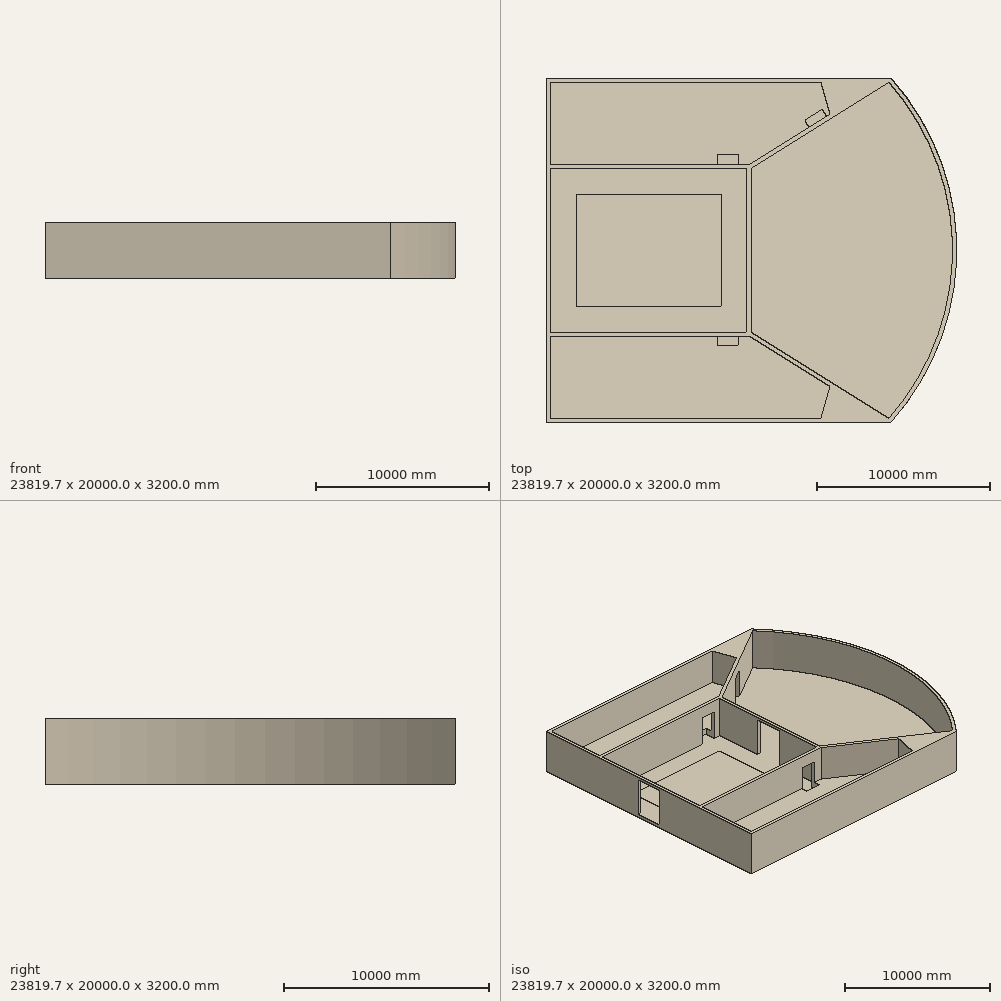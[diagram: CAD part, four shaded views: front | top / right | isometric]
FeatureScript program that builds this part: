
annotation { "Feature Type Name" : "Feature", "Feature Type Description" : "" }
export const myFeature = defineFeature(function(context is Context, id is Id, definition is map)
    precondition{}
    {
        {
            var Q0;
            Q0=qCreatedBy(makeId("Top.planeOp"),FACE);
            var sketch = newSketch(context, id + "F0", { "sketchPlane" : qUnion([Q0])});
            skLineSegment(sketch, "E0.bottom", {"start": v(0, 0) * mm, "end": v(20000, 0) * mm});
            skLineSegment(sketch, "E0.top", {"start": v(0, 20000) * mm, "end": v(20000, 20000) * mm});
            skLineSegment(sketch, "E0.left", {"start": v(0, 0) * mm, "end": v(0, 20000) * mm});
            skLineSegment(sketch, "E0.right", {"start": v(20000, 0) * mm, "end": v(20000, 20000) * mm});
            skLineSegment(sketch, "E1", {"start": v(20000, 10000) * mm, "end": v(8819.66, 10000) * mm});
            skCircle(sketch, "E2", {"center": v(8819.66, 10000) * mm, "radius": 15000 * mm});
            skSolve(sketch);
        }
        {
            var Q0;
            {var subQ2=sQuery(id+"F0.wireOp",EDGE,"E0.bottom");Q0=makeQuery(id+"F0.imprint","IMPRINT",FACE,{"disambiguationData":[TD([[makeQuery(id+"F0.imprint","IMPRINT",EDGE,{"derivedFrom":subQ2}),1.0]])]});}
            var Q1;
            {var subQ1=sQuery(id+"F0.wireOp",EDGE,"E0.right");var subQ3=makeQuery(id+"F0.imprint","IMPRINT",VERTEX,{"derivedFrom":subQ1});Q1=makeQuery(id+"F0.imprint","IMPRINT",FACE,{"disambiguationData":[TD([[makeQuery(id+"F0.imprint","IMPRINT",EDGE,{"disambiguationData":[TD([[subQ3,1.0]])],"derivedFrom":subQ1}),-1.0]])]});}
            extrude(context, id + "F1", {"entities" : qUnion([Q0, Q1]), "depth" : 3200 * mm});
        }
        {
            var Q0;
            Q0=makeQuery(id+"F1.opExtrude","CAP_FACE",FACE,{"disambiguationData":[OSD([sQuery(id+"F0.wireOp",EDGE,"E0.bottom"),sQuery(id+"F0.wireOp",EDGE,"E0.top"),sQuery(id+"F0.wireOp",EDGE,"E0.left"),sQuery(id+"F0.wireOp",EDGE,"E2")])],"isStart":false});
            var sketch = newSketch(context, id + "F2", { "sketchPlane" : qUnion([Q0])});
            skLineSegment(sketch, "E3.0", {"start": v(250, 250) * mm, "end": v(19887.63, 250) * mm});
            skLineSegment(sketch, "E3.1", {"start": v(250, 19750) * mm, "end": v(250, 250) * mm});
            skLineSegment(sketch, "E3.2", {"start": v(19887.63, 19750) * mm, "end": v(250, 19750) * mm});
            skArc(sketch, "E3.3", {"start": v(19887.63, 250) * mm, "mid": v(23569.66, 10000) * mm, "end": v(19887.63, 19750) * mm});
            skLineSegment(sketch, "E4", {"start": v(19887.63, 19750) * mm, "end": v(11887.63, 14750) * mm});
            skLineSegment(sketch, "E5", {"start": v(11887.63, 14750) * mm, "end": v(11887.63, 5250) * mm});
            skLineSegment(sketch, "E6", {"start": v(11887.63, 5250) * mm, "end": v(19887.63, 250) * mm});
            skLineSegment(sketch, "E7", {"start": v(11887.63, 14750) * mm, "end": v(250, 14750) * mm});
            skLineSegment(sketch, "E8", {"start": v(11887.63, 5250) * mm, "end": v(250, 5250) * mm});
            skLineSegment(sketch, "E9.0", {"start": v(11815.93, 15000) * mm, "end": v(250, 15000) * mm});
            skLineSegment(sketch, "E9.1", {"start": v(19415.93, 19750) * mm, "end": v(11815.93, 15000) * mm});
            skLineSegment(sketch, "E10.0", {"start": v(11815.93, 5000) * mm, "end": v(250, 5000) * mm});
            skLineSegment(sketch, "E10.1", {"start": v(11815.93, 5000) * mm, "end": v(19415.93, 250) * mm});
            skLineSegment(sketch, "E11.0", {"start": v(11637.63, 14750) * mm, "end": v(11637.63, 5250) * mm});
            skSolve(sketch);
        }
        {
            var Q0;
            Q0=makeQuery(id+"F2.imprint","IMPRINT",FACE,{"disambiguationData":[TD([[makeQuery(id+"F2.imprint","IMPRINT",EDGE,{"derivedFrom":sQuery(id+"F2.wireOp",EDGE,"E3.3")}),1.0]])]});
            var Q1;
            {var subQ5=sQuery(id+"F2.wireOp",EDGE,"E11.0");Q1=makeQuery(id+"F2.imprint","IMPRINT",FACE,{"disambiguationData":[TD([[makeQuery(id+"F2.imprint","IMPRINT",EDGE,{"derivedFrom":subQ5}),-1.0]])]});}
            extrude(context, id + "F3", {"entities" : qUnion([Q0, Q1]), "operationType" : NewBodyOperationType.REMOVE, "oppositeDirection" : true, "depth" : 2950 * mm});
        }
        {
            var Q0;
            {var subQ3=sQuery(id+"F2.wireOp",EDGE,"E9.0");Q0=makeQuery(id+"F2.imprint","IMPRINT",FACE,{"disambiguationData":[TD([[makeQuery(id+"F2.imprint","IMPRINT",EDGE,{"derivedFrom":subQ3}),-1.0]])]});}
            var Q1;
            {var subQ4=sQuery(id+"F2.wireOp",EDGE,"E10.0");Q1=makeQuery(id+"F2.imprint","IMPRINT",FACE,{"disambiguationData":[TD([[makeQuery(id+"F2.imprint","IMPRINT",EDGE,{"derivedFrom":subQ4}),1.0]])]});}
            extrude(context, id + "F4", {"entities" : qUnion([Q0, Q1]), "operationType" : NewBodyOperationType.REMOVE, "oppositeDirection" : true, "depth" : 2500 * mm});
        }
        {
            var Q0;
            Q0=makeQuery(id+"F1.opExtrude","SWEPT_FACE",FACE,{"disambiguationData":[OSD([sQuery(id+"F0.wireOp",EDGE,"E0.left")])]});
            var sketch = newSketch(context, id + "F5", { "sketchPlane" : qUnion([Q0])});
            skLineSegment(sketch, "E12", {"start": v(-10000, 0) * mm, "end": v(-10000, 1500) * mm});
            skLineSegment(sketch, "E13.bottom", {"start": v(-8950, 0) * mm, "end": v(-11050, 0) * mm});
            skLineSegment(sketch, "E13.top", {"start": v(-8950, 3000) * mm, "end": v(-11050, 3000) * mm});
            skLineSegment(sketch, "E13.left", {"start": v(-8950, 0) * mm, "end": v(-8950, 3000) * mm});
            skLineSegment(sketch, "E13.right", {"start": v(-11050, 0) * mm, "end": v(-11050, 3000) * mm});
            skPoint(sketch, "E13.middle", {"position": v(-10000, 1500) * mm});
            skLineSegment(sketch, "E14", {"start": v(-11050, 250) * mm, "end": v(-8950, 250) * mm});
            skSolve(sketch);
        }
        {
            var Q0;
            {var subQ5=sQuery(id+"F5.wireOp",EDGE,"E13.top");Q0=makeQuery(id+"F5.imprint","IMPRINT",FACE,{"disambiguationData":[TD([[makeQuery(id+"F5.imprint","IMPRINT",EDGE,{"derivedFrom":subQ5}),1.0]])]});}
            extrude(context, id + "F6", {"entities" : qUnion([Q0]), "operationType" : NewBodyOperationType.REMOVE, "oppositeDirection" : true, "depth" : 15000 * mm});
        }
        {
            var Q0;
            Q0=makeQuery(id+"F1.opExtrude","SWEPT_FACE",FACE,{"disambiguationData":[OSD([sQuery(id+"F0.wireOp",EDGE,"E0.left")])]});
            var sketch = newSketch(context, id + "F7", { "sketchPlane" : qUnion([Q0])});
            skLineSegment(sketch, "E15", {"start": v(-11050, 250) * mm, "end": v(-11050, 0) * mm});
            skLineSegment(sketch, "E16", {"start": v(-8950, 250) * mm, "end": v(-8950, 0) * mm});
            skLineSegment(sketch, "E17", {"start": v(-8950, 125) * mm, "end": v(-11050, 125) * mm});
            skSolve(sketch);
        }
        {
            var Q0;
            Q0=makeQuery(id+"F3.boolean.opBoolean","COPY",FACE,{"derivedFrom":makeQuery(id+"F3.opExtrude","SWEPT_FACE",FACE,{"disambiguationData":[OSD([sQuery(id+"F2.wireOp",EDGE,"E8")])]})});
            var sketch = newSketch(context, id + "F8", { "sketchPlane" : qUnion([Q0])});
            skLineSegment(sketch, "E18.bottom", {"start": v(-11137.63, 250) * mm, "end": v(-9937.63, 250) * mm});
            skLineSegment(sketch, "E18.top", {"start": v(-11137.63, 2350) * mm, "end": v(-9937.63, 2350) * mm});
            skLineSegment(sketch, "E18.left", {"start": v(-11137.63, 250) * mm, "end": v(-11137.63, 2350) * mm});
            skLineSegment(sketch, "E18.right", {"start": v(-9937.63, 250) * mm, "end": v(-9937.63, 2350) * mm});
            skSolve(sketch);
        }
        {
            var Q0;
            Q0 = qSketchRegion(id + "F8", true);
            extrude(context, id + "F9", {"entities" : qUnion([Q0]), "operationType" : NewBodyOperationType.REMOVE, "oppositeDirection" : true, "depth" : 750 * mm, "hasSecondDirection" : true, "secondDirectionOppositeDirection" : false, "secondDirectionDepth" : 10300 * mm});
        }
        {
            var Q0;
            Q0=makeQuery(id+"F1.opExtrude","SWEPT_FACE",FACE,{"disambiguationData":[OSD([sQuery(id+"F0.wireOp",EDGE,"E0.top")])]});
            var Q1;
            Q1=makeQuery(id+"F1.opExtrude","SWEPT_FACE",FACE,{"disambiguationData":[OSD([sQuery(id+"F0.wireOp",EDGE,"E0.bottom")])]});
            cPlane(context, id + "F10", {"entities" : qUnion([Q0, Q1]), "cplaneType" : CPlaneType.MID_PLANE, "offset" : 25 * mm, "width" : 150 * mm, "height" : 150 * mm});
        }
        {
            var Q0;
            Q0=makeQuery(id+"F3.boolean.opBoolean","COPY",FACE,{"derivedFrom":makeQuery(id+"F3.opExtrude","SWEPT_FACE",FACE,{"disambiguationData":[OSD([sQuery(id+"F2.wireOp",EDGE,"E4")])]})});
            var sketch = newSketch(context, id + "F11", { "sketchPlane" : qUnion([Q0])});
            skLineSegment(sketch, "E19", {"start": v(22615.17, 250) * mm, "end": v(22615.17, 1300) * mm});
            skLineSegment(sketch, "E20.bottom", {"start": v(22015.17, 250) * mm, "end": v(23215.17, 250) * mm});
            skLineSegment(sketch, "E20.top", {"start": v(22015.17, 2350) * mm, "end": v(23215.17, 2350) * mm});
            skLineSegment(sketch, "E20.left", {"start": v(22015.17, 250) * mm, "end": v(22015.17, 2350) * mm});
            skLineSegment(sketch, "E20.right", {"start": v(23215.17, 250) * mm, "end": v(23215.17, 2350) * mm});
            skPoint(sketch, "E20.middle", {"position": v(22615.17, 1300) * mm});
            skSolve(sketch);
        }
        {
            var Q0;
            Q0 = qSketchRegion(id + "F11", true);
            extrude(context, id + "F12", {"entities" : qUnion([Q0]), "operationType" : NewBodyOperationType.REMOVE, "oppositeDirection" : true, "depth" : 725 * mm});
        }
        {
            var Q0;
            {var subQ0=sQuery(id+"F11.wireOp",EDGE,"E20.bottom");Q0=makeQuery(id+"FxmqvzjOIRDMaaB_1.1.F12.boolean.opBoolean","MERGE",FACE,{"derivedFrom":[makeQuery(id+"F12.boolean.opBoolean","MERGE",FACE,{"derivedFrom":[makeQuery(id+"F9.boolean.opBoolean","MERGE",FACE,{"derivedFrom":[makeQuery(id+"F6.boolean.opBoolean","MERGE",FACE,{"derivedFrom":[makeQuery(id+"F3.boolean.opBoolean","COPY",FACE,{"derivedFrom":makeQuery(id+"F3.opExtrude","CAP_FACE",FACE,{"disambiguationData":[OSD([sQuery(id+"F2.wireOp",EDGE,"E3.1"),sQuery(id+"F2.wireOp",EDGE,"E7"),sQuery(id+"F2.wireOp",EDGE,"E8"),sQuery(id+"F2.wireOp",EDGE,"E11.0")])],"isStart":false})}),makeQuery(id+"F3.boolean.opBoolean","COPY",FACE,{"derivedFrom":makeQuery(id+"F3.opExtrude","CAP_FACE",FACE,{"disambiguationData":[OSD([sQuery(id+"F2.wireOp",EDGE,"E3.3"),sQuery(id+"F2.wireOp",EDGE,"E4"),sQuery(id+"F2.wireOp",EDGE,"E5"),sQuery(id+"F2.wireOp",EDGE,"E6")])],"isStart":false})}),makeQuery(id+"F6.opExtrude","SWEPT_FACE",FACE,{"disambiguationData":[OSD([sQuery(id+"F5.wireOp",EDGE,"E14")])]})]}),makeQuery(id+"F9.opExtrude","SWEPT_FACE",FACE,{"disambiguationData":[OSD([sQuery(id+"F8.wireOp",EDGE,"E18.bottom")])]})]}),makeQuery(id+"F12.opExtrude","SWEPT_FACE",FACE,{"disambiguationData":[OSD([subQ0])]})]}),makeQuery(id+"FxmqvzjOIRDMaaB_1.1.F12.opExtrude","SWEPT_FACE",FACE,{"disambiguationData":[OSD([subQ0])]})]});}
            var sketch = newSketch(context, id + "F13", { "sketchPlane" : qUnion([Q0])});
            skLineSegment(sketch, "E21.bottom", {"start": v(250, 14750) * mm, "end": v(11637.63, 14750) * mm});
            skLineSegment(sketch, "E21.top", {"start": v(250, 5250) * mm, "end": v(11637.63, 5250) * mm});
            skLineSegment(sketch, "E21.left", {"start": v(250, 14750) * mm, "end": v(250, 5250) * mm});
            skLineSegment(sketch, "E21.right", {"start": v(11637.63, 14750) * mm, "end": v(11637.63, 5250) * mm});
            skLineSegment(sketch, "E22.0", {"start": v(1750, 13250) * mm, "end": v(1750, 6750) * mm});
            skLineSegment(sketch, "E22.1", {"start": v(1750, 13250) * mm, "end": v(10137.63, 13250) * mm});
            skLineSegment(sketch, "E22.2", {"start": v(10137.63, 13250) * mm, "end": v(10137.63, 6750) * mm});
            skLineSegment(sketch, "E22.3", {"start": v(1750, 6750) * mm, "end": v(10137.63, 6750) * mm});
            skSolve(sketch);
        }
        {
            var Q0;
            Q0=makeQuery(id+"F13.imprint","IMPRINT",FACE,{"disambiguationData":[TD([[makeQuery(id+"F13.imprint","IMPRINT",EDGE,{"derivedFrom":sQuery(id+"F13.wireOp",EDGE,"E22.0")}),1.0]])]});
            extrude(context, id + "F14", {"entities" : qUnion([Q0]), "depth" : 15 * mm});
        }
        {
            var Q0;
            Q0=makeQuery(id+"F4.boolean.opBoolean","COPY",EDGE,{"derivedFrom":makeQuery(id+"F4.opExtrude","SWEPT_EDGE",EDGE,{"disambiguationData":[OSD([sQuery(id+"F2.wireOp",EDGE,"E3.2"),sQuery(id+"F2.wireOp",EDGE,"E9.1")])]})});
            var Q1;
            Q1=makeQuery(id+"F4.boolean.opBoolean","COPY",EDGE,{"derivedFrom":makeQuery(id+"F4.opExtrude","SWEPT_EDGE",EDGE,{"disambiguationData":[OSD([sQuery(id+"F2.wireOp",EDGE,"E3.0"),sQuery(id+"F2.wireOp",EDGE,"E10.1")])]})});
            chamfer(context, id + "F15", {"entities" : qUnion([Q0, Q1]), "width" : 1000 * mm, "tangentPropagation" : true});
        }
    });
